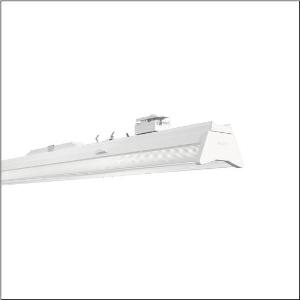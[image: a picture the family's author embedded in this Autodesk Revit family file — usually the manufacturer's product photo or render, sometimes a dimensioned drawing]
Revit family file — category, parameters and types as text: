
# Revit family: licross_11_performance_mo_51tm16dn4axg
name_source: partatom
category: Lighting Fixtures
units: mm (PartAtom-declared; Revit-internal decimal feet)

## family parameters
Cut with Voids When Loaded = No
Host = Face
Light Source = No
Part Type = Normal
Room Calculation Point = No
Round Connector Dimension = Use Diameter
Shared = No

## types (1)
- --- (1 x LED, 10110 lm, 57.1 W, 4000K)
    Apparent Load = 57 VA
    CIE Flux Codes = 66 88 96 79 100
    Color Rendering = 80
    Color Temperature = 4000K
    Default Elevation = 1800 mm
    Description = Licross 11 Performance MO, luminaire insert, of sheet steel, galvanised, coil coated, white, length: 1.500mm, width: 120mm, height: 123mm, LED rated luminous flux: 10.110lm, light colour: 840, SDCM (Standard Deviation of Colour Matching)MacAdam ≤ 2 SDCM (initial), control gear: DALI 2, with plug, 5-pole, with phase selection, mains connection: 220..240V, AC, 50/60Hz, rated input power: 57W, internal wiring halogen-free, primary light control with lens, of plastic, primary optical cover: cover, of PMMA, light emission: direct/indirect distribution, primary light characteristic: symmetric, protection rating (complete): IP40, insulation class (complete): insulation class I (protective earthing), certification: CE, ENEC, VDE, UKCA, protection symbol: D if used in an environment without relevant dust loads with corresponding accessories, impact resistance: IK06, permissible ambient temperature for indoor applications: -25..+35°C, corresponds to IFS (International Featured Standards) requirements for safety and quality in the food industry, reducing of maximum allowable ambient temperature of 5°C with ceiling mounting, LABS conformity tested according to VDMA 24364:2018-05, The light source and the operating device comply with the requirements of the Ecodesign Regulation (EU) 2019/2020 and are replaceable in accordance with this regulation, packaging unit: 1 piece
    Height = 114 mm
    Lamp = 1 x LED
    Lamp Light Flux = 10110 lm
    Lamp Power = 57.1 W
    Lamp count = 1
    Length = 1500 mm
    Luminous efficacy = 177 lm/W
    Manufacturer = Siteco
    ModVariant = No
    Model = 51TM16DN4AXG
    Mounting Place = Ceiling
    Mounting Type = Pendant
    Number of Poles = 1
    OnlyDefault = Yes
    Power Factor = 1
    Product Name = Licross 11 Performance MO
    Product group = luminaire insert | ceiling pendant
    ProductGroupID = 901
    Protection Class = Protection class I
    Protection Degree = IP 40
    RLX_Detail_Level = 1
    RLX_Emergency_Light_Flux = 0 lm
    RLX_Emergency_Type = 0
    RLX_Emergency_Type_DB = No
    RlxData = <blob elided: 34349 chars, md5=8b739d48>
    Socket = socket
    Standby Power = 0 W
    System Light Flux = 10110 lm
    System Power = 57 W
    Type Comments = factory setting: luminous flux: 100 % | dim-lin: 254 | 378 mA
    Type Image = l_1256138.jpg
    URL = http://relux.com
    VarID = @adj_104449
    Voltage = 0 V
    Weight = 0.00 kg
    Width = 120 mm

## geometry (parser evidence)
native form markers: Blend x4, Sweep x11
no freeform markers — native parametric forms only
